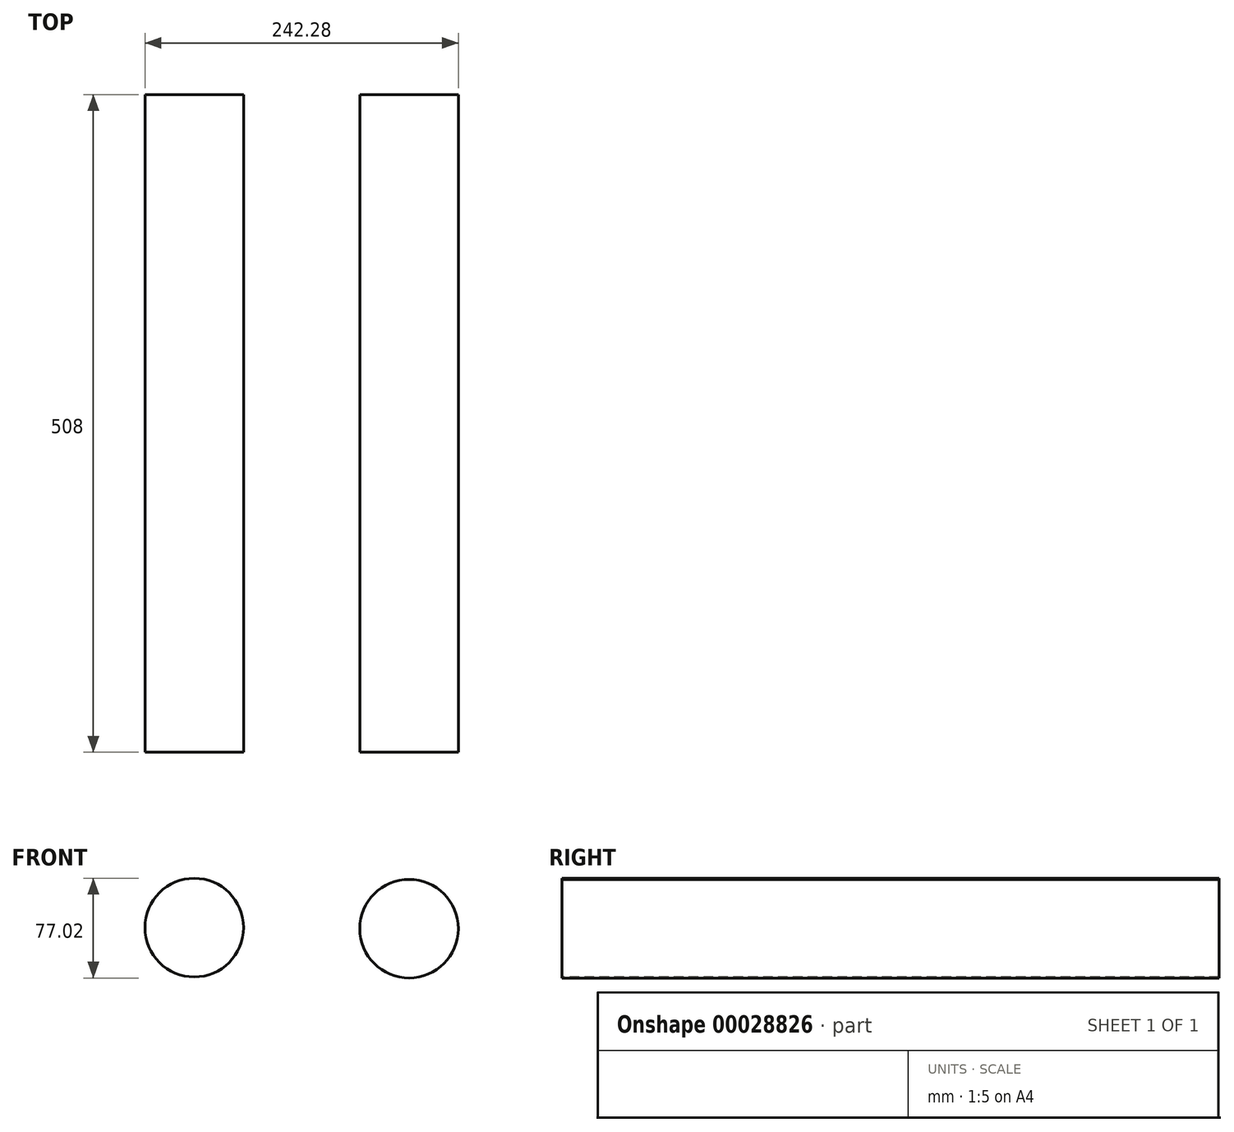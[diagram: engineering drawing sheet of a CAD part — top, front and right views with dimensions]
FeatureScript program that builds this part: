
annotation { "Feature Type Name" : "Feature", "Feature Type Description" : "" }
export const myFeature = defineFeature(function(context is Context, id is Id, definition is map)
    precondition{}
    {
        {
            var Q0;
            Q0=qCreatedBy(makeId("Front.planeOp"),FACE);
            var sketch = newSketch(context, id + "F0", { "sketchPlane" : qUnion([Q0])});
            skCircle(sketch, "E0", {"center": v(-90.18, 0.82) * mm, "radius": 38.1 * mm});
            skCircle(sketch, "E1", {"center": v(75.9, 0) * mm, "radius": 38.1 * mm});
            skSolve(sketch);
        }
        {
            var Q0;
            Q0 = qSketchRegion(id + "F0", true);
            extrude(context, id + "F1", {"entities" : qUnion([Q0]), "oppositeDirection" : true, "depth" : 508 * mm});
        }
    });
